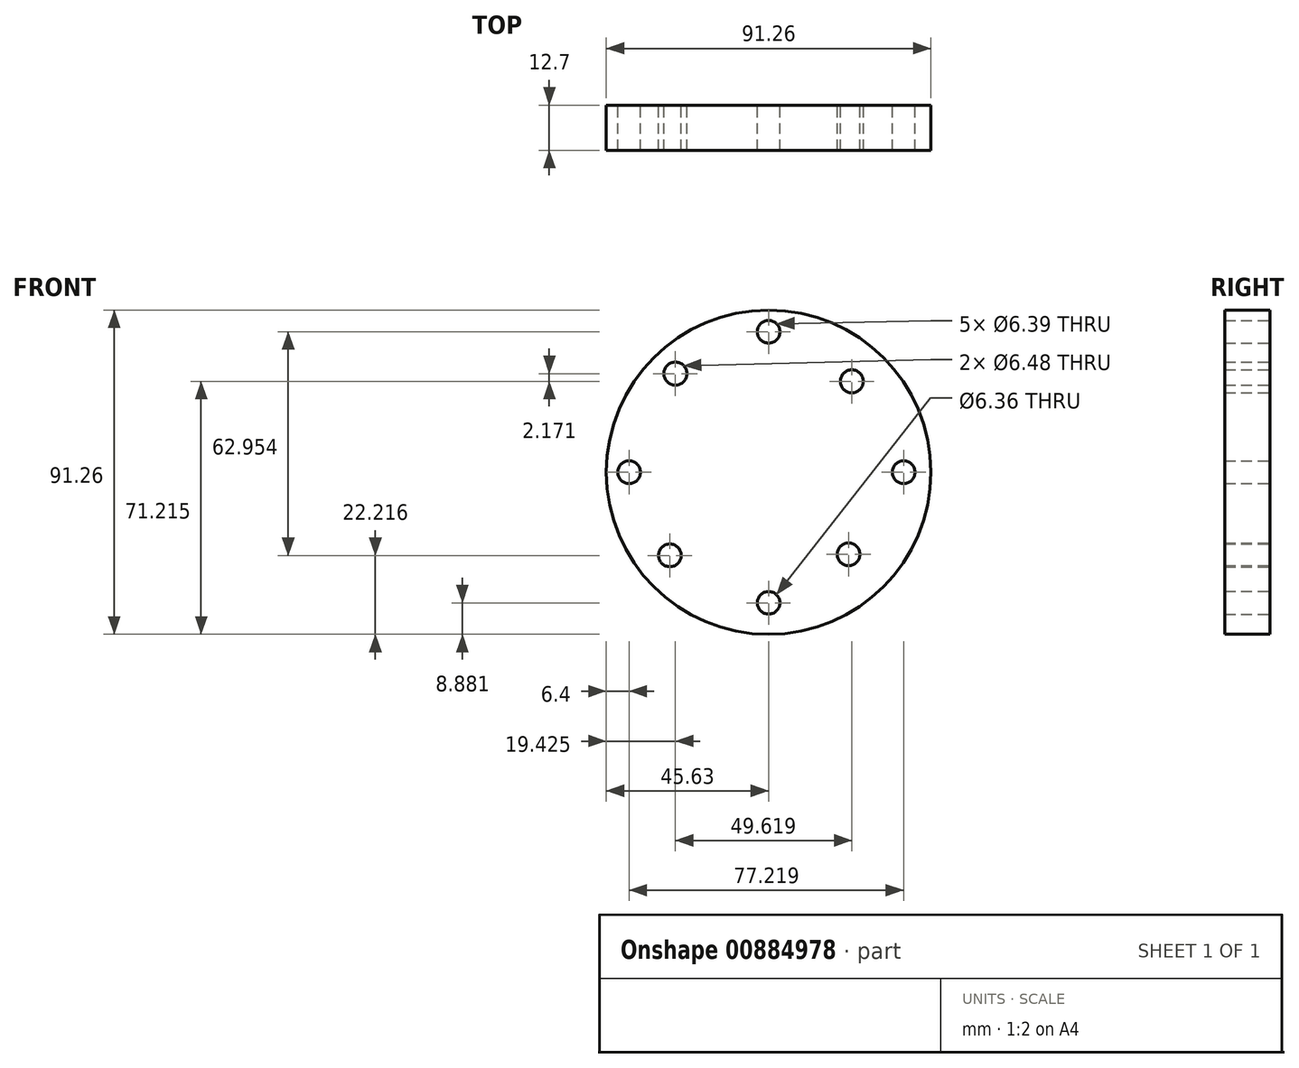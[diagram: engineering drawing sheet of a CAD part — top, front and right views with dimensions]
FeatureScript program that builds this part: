
annotation { "Feature Type Name" : "Feature", "Feature Type Description" : "" }
export const myFeature = defineFeature(function(context is Context, id is Id, definition is map)
    precondition{}
    {
        {
            var Q0;
            Q0=qCreatedBy(makeId("Front.planeOp"),FACE);
            var sketch = newSketch(context, id + "F0", { "sketchPlane" : qUnion([Q0])});
            skCircle(sketch, "E0", {"center": v(0, 0) * mm, "radius": 45.63 * mm});
            skSolve(sketch);
        }
        {
            var Q0;
            Q0 = qSketchRegion(id + "F0", true);
            extrude(context, id + "F1", {"entities" : qUnion([Q0]), "depth" : 12.7 * mm, "offsetDistance" : 25.4 * mm});
        }
        {
            var Q0;
            Q0=qCreatedBy(makeId("Front.planeOp"),FACE);
            var sketch = newSketch(context, id + "F2", { "sketchPlane" : qUnion([Q0])});
            skCircle(sketch, "E1", {"center": v(0, 39.54) * mm, "radius": 3.2 * mm});
            skCircle(sketch, "E2", {"center": v(37.99, 0) * mm, "radius": 3.2 * mm});
            skCircle(sketch, "E3", {"center": v(0, -36.75) * mm, "radius": 3.18 * mm});
            skCircle(sketch, "E4", {"center": v(-39.23, 0) * mm, "radius": 3.2 * mm});
            skCircle(sketch, "E5", {"center": v(-26.2, 27.76) * mm, "radius": 3.24 * mm});
            skCircle(sketch, "E6", {"center": v(-27.76, -23.41) * mm, "radius": 3.2 * mm});
            skCircle(sketch, "E7", {"center": v(23.41, 25.58) * mm, "radius": 3.24 * mm});
            skCircle(sketch, "E8", {"center": v(22.48, -23.1) * mm, "radius": 3.2 * mm});
            skSolve(sketch);
        }
        {
            var Q0;
            Q0 = qSketchRegion(id + "F2", true);
            extrude(context, id + "F3", {"entities" : qUnion([Q0]), "operationType" : NewBodyOperationType.REMOVE, "depth" : 25.4 * mm, "offsetDistance" : 25.4 * mm});
        }
    });
